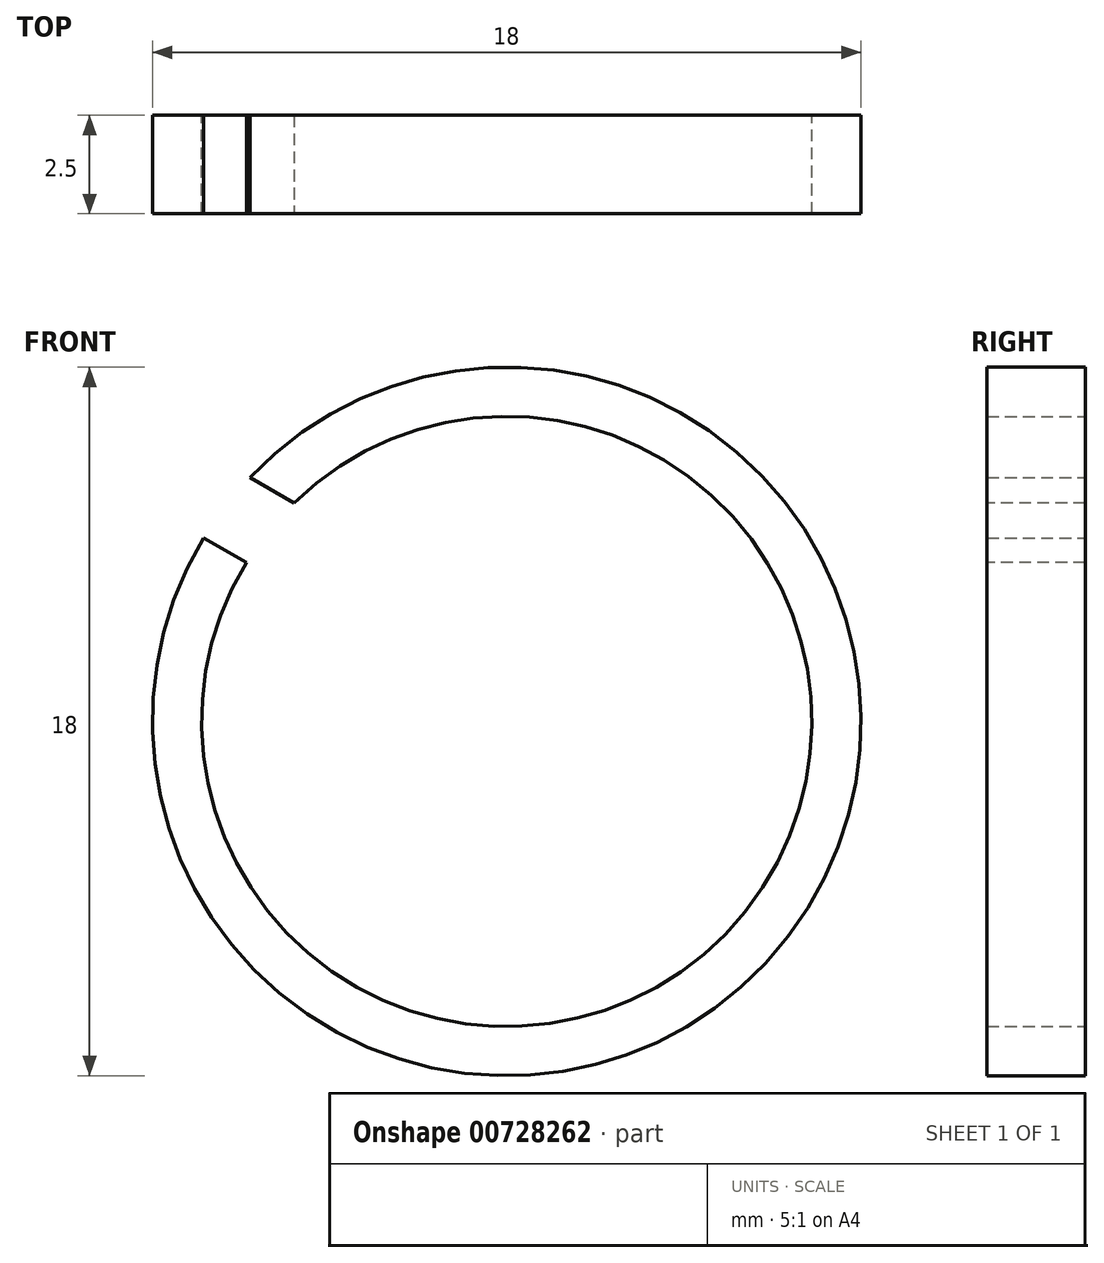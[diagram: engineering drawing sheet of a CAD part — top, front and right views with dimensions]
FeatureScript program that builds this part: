
annotation { "Feature Type Name" : "Feature", "Feature Type Description" : "" }
export const myFeature = defineFeature(function(context is Context, id is Id, definition is map)
    precondition{}
    {
        {
            var Q0;
            Q0=qCreatedBy(makeId("Front.planeOp"),FACE);
            var sketch = newSketch(context, id + "F0", { "sketchPlane" : qUnion([Q0])});
            skCircle(sketch, "E0", {"center": v(0, 0) * mm, "radius": 9 * mm});
            skCircle(sketch, "E1", {"center": v(0, 0) * mm, "radius": 7.75 * mm});
            skSolve(sketch);
        }
        {
            var Q0;
            Q0 = qSketchRegion(id + "F0", true);
            extrude(context, id + "F1", {"entities" : qUnion([Q0]), "depth" : 2.5 * mm, "offsetDistance" : 25 * mm});
        }
        {
            var Q0;
            Q0=makeQuery(id+"F1.opExtrude","CAP_FACE",FACE,{"disambiguationData":[OSD([sQuery(id+"F0.wireOp",EDGE,"E0"),sQuery(id+"F0.wireOp",EDGE,"E1")])],"isStart":false});
            var sketch = newSketch(context, id + "F2", { "sketchPlane" : qUnion([Q0])});
            skLineSegment(sketch, "E2", {"start": v(-7.7, 4.67) * mm, "end": v(-6.61, 4.04) * mm});
            skLineSegment(sketch, "E3", {"start": v(-6.61, 4.04) * mm, "end": v(-5.4, 5.55) * mm});
            skLineSegment(sketch, "E4", {"start": v(-5.4, 5.55) * mm, "end": v(-6.53, 6.2) * mm});
            skLineSegment(sketch, "E5", {"start": v(-6.53, 6.2) * mm, "end": v(-7.7, 4.67) * mm});
            skSolve(sketch);
        }
        {
            var Q0;
            Q0 = qSketchRegion(id + "F2", true);
            extrude(context, id + "F3", {"entities" : qUnion([Q0]), "operationType" : NewBodyOperationType.REMOVE, "oppositeDirection" : true, "depth" : 25 * mm, "offsetDistance" : 25 * mm});
        }
        {
            var Q0;
            {var subQ0=sQuery(id+"F0.wireOp",EDGE,"E0");Q0=makeQuery(id+"F3.boolean.opBoolean","SPLIT",FACE,{"disambiguationData":[TD([makeQuery(id+"F3.opExtrude","SWEPT_FACE",FACE,{"disambiguationData":[OSD([sQuery(id+"F2.wireOp",EDGE,"E5")])]})])],"derivedFrom":makeQuery(id+"F1.opExtrude","CAP_FACE",FACE,{"disambiguationData":[OSD([subQ0,sQuery(id+"F0.wireOp",EDGE,"E1")])],"isStart":false})});}
            var sketch = newSketch(context, id + "F4", { "sketchPlane" : qUnion([Q0])});
            skLineSegment(sketch, "E6.bottom", {"start": v(-6.53, 6.2) * mm, "end": v(-8.32, 6.2) * mm});
            skLineSegment(sketch, "E6.top", {"start": v(-6.53, 5.73) * mm, "end": v(-8.32, 5.73) * mm});
            skLineSegment(sketch, "E6.left", {"start": v(-6.53, 6.2) * mm, "end": v(-6.53, 5.73) * mm});
            skLineSegment(sketch, "E6.right", {"start": v(-8.32, 6.2) * mm, "end": v(-8.32, 5.73) * mm});
            skSolve(sketch);
        }
        {
            var Q0;
            Q0 = qSketchRegion(id + "F4", true);
            extrude(context, id + "F5", {"entities" : qUnion([Q0]), "operationType" : NewBodyOperationType.REMOVE, "oppositeDirection" : true, "depth" : 25 * mm, "offsetDistance" : 25 * mm});
        }
        {
            var Q0;
            {var subQ0=sQuery(id+"F0.wireOp",EDGE,"E0");Q0=makeQuery(id+"F3.boolean.opBoolean","SPLIT",FACE,{"disambiguationData":[TD([makeQuery(id+"F3.opExtrude","SWEPT_FACE",FACE,{"disambiguationData":[OSD([sQuery(id+"F2.wireOp",EDGE,"E5")])]})])],"derivedFrom":makeQuery(id+"F1.opExtrude","CAP_FACE",FACE,{"disambiguationData":[OSD([subQ0,sQuery(id+"F0.wireOp",EDGE,"E1")])],"isStart":false})});}
            var sketch = newSketch(context, id + "F6", { "sketchPlane" : qUnion([Q0])});
            skLineSegment(sketch, "E7.bottom", {"start": v(-7.7, 4.67) * mm, "end": v(-6.66, 4.67) * mm});
            skLineSegment(sketch, "E7.top", {"start": v(-7.7, 6.06) * mm, "end": v(-6.66, 6.06) * mm});
            skLineSegment(sketch, "E7.left", {"start": v(-7.7, 4.67) * mm, "end": v(-7.7, 6.06) * mm});
            skLineSegment(sketch, "E7.right", {"start": v(-6.66, 4.67) * mm, "end": v(-6.66, 6.06) * mm});
            skSolve(sketch);
        }
        {
            var Q0;
            Q0 = qSketchRegion(id + "F6", true);
            extrude(context, id + "F7", {"entities" : qUnion([Q0]), "operationType" : NewBodyOperationType.REMOVE, "oppositeDirection" : true, "depth" : 25 * mm, "offsetDistance" : 25 * mm});
        }
    });
